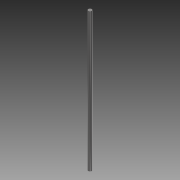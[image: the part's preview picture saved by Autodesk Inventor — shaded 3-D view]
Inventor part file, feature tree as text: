
AUTODESK INVENTOR PART (.ipt)
format: ipt  version: 2013 (Build 170138000, 138)  size: 73,728 bytes
history: native  units: mm
features: extrude x1, sketch x1
ambient origin geometry x8: Origin, YZ Plane, XZ Plane, XY Plane, X Axis, Y Axis, Z Axis, Center Point
bodies: Solid1 (feature_tree)
feature tree (2):
  extrude  "Extrusion1"  Depth=325.0mm TaperAngle=0.0deg
  sketch  "Sketch1"  dims[d0=8.0mm d2=325.0mm d3=0.0mm]
